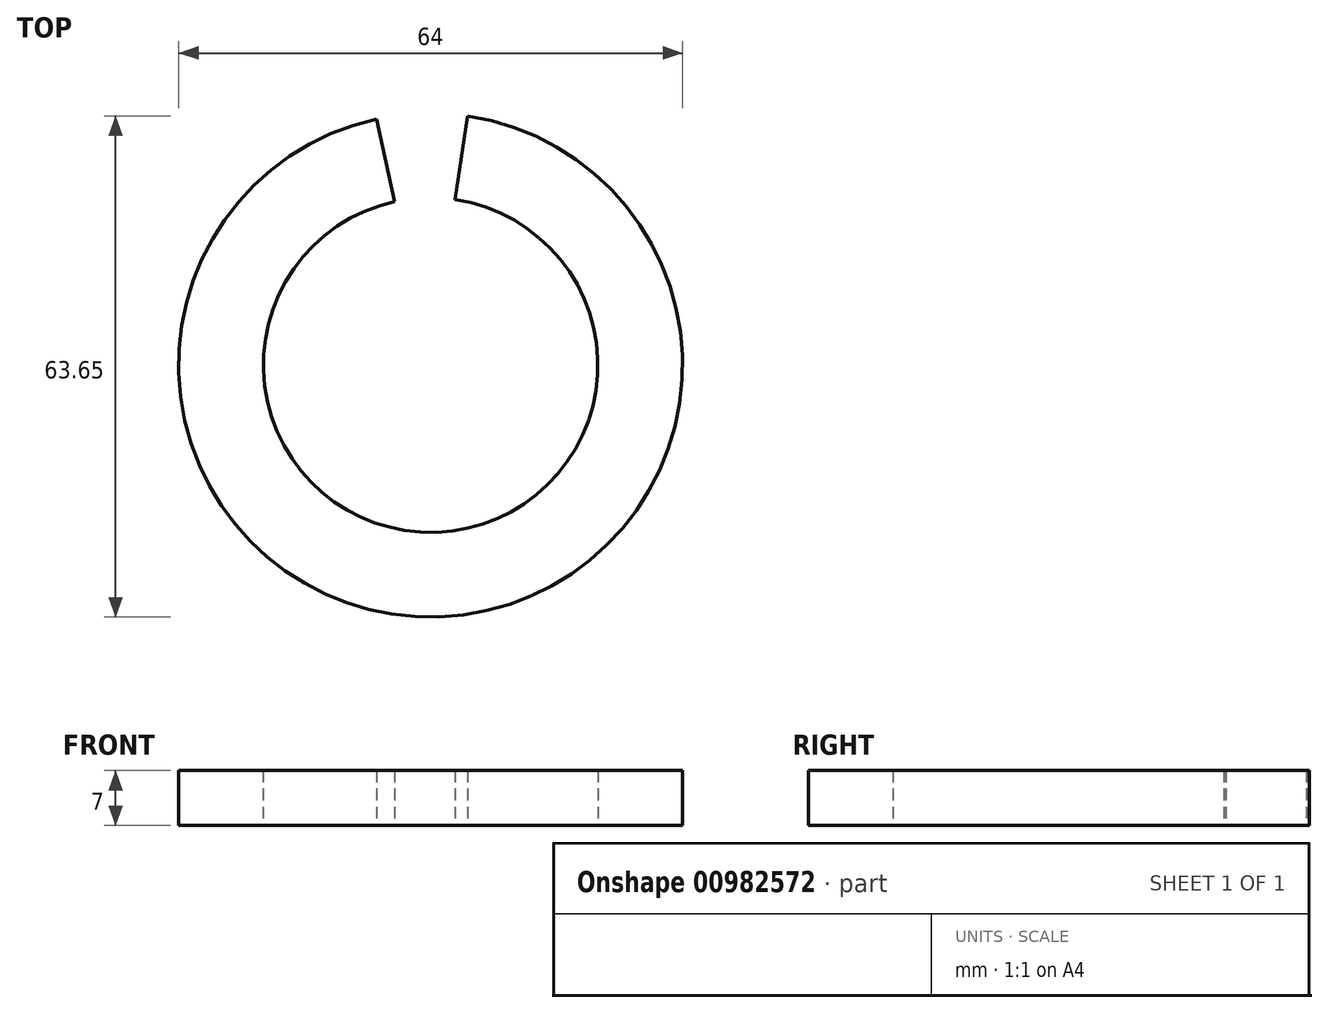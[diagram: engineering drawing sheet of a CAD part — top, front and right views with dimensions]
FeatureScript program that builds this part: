
annotation { "Feature Type Name" : "Feature", "Feature Type Description" : "" }
export const myFeature = defineFeature(function(context is Context, id is Id, definition is map)
    precondition{}
    {
        {
            var Q0;
            Q0=qCreatedBy(makeId("Top.planeOp"),FACE);
            var sketch = newSketch(context, id + "F0", { "sketchPlane" : qUnion([Q0])});
            skArc(sketch, "E0", {"start": v(-4.58, 20.75) * mm, "mid": v(0.73, -21.24) * mm, "end": v(3.14, 21.02) * mm});
            skArc(sketch, "E1", {"start": v(-6.9, 31.25) * mm, "mid": v(1.1, -31.98) * mm, "end": v(4.72, 31.65) * mm});
            skLineSegment(sketch, "E2", {"start": v(-4.58, 20.75) * mm, "end": v(-6.9, 31.25) * mm});
            skLineSegment(sketch, "E3", {"start": v(3.14, 21.02) * mm, "end": v(4.72, 31.65) * mm});
            skSolve(sketch);
        }
        {
            var Q0;
            Q0=makeQuery(id+"F0.imprint","IMPRINT",FACE,{"disambiguationData":[TD([[makeQuery(id+"F0.imprint","IMPRINT",EDGE,{"derivedFrom":sQuery(id+"F0.wireOp",EDGE,"E0")}),-1.0]])]});
            extrude(context, id + "F1", {"entities" : qUnion([Q0]), "depth" : 7 * mm, "offsetDistance" : 25 * mm});
        }
    });
